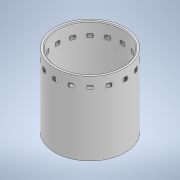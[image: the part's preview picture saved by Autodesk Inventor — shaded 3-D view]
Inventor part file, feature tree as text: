
AUTODESK INVENTOR PART (.ipt)
format: ipt  version: 2022.4 (Build 264492010, 492A)  size: 337,920 bytes
history: native  units: mm
features: extrude x2, sketch x2, fillet x1, chamfer x1, pattern_circular x1, plane x1
ambient origin geometry x8: Origin, YZ Plane, XZ Plane, XY Plane, X Axis, Y Axis, Z Axis, Center Point
bodies: Solid1 (feature_tree)
feature tree (8):
  extrude  "Extrusion1"  Depth=95.0mm TaperAngle=0.0deg
  extrude  "Extrusion3"  Depth=1.0mm
  fillet  "Fillet1"  [1 undecoded]
  chamfer  "Chamfer1"  Distance=10.0mm
  pattern_circular  "Circular Pattern2"  [2 undecoded]
  plane  "Work Plane1"
  sketch  "Sketch1"  dims[d0=84.05mm d2=95.0mm d3=0.0mm]
  sketch  "Sketch2"  dims[d4=5.0mm d5=5.0mm d8=45.0deg d9=10.0mm d10=6.0mm d11=0.0mm d12=1.0mm d16=1.0mm d17=2.0mm d18=45.0deg d19=160.0mm d20=360.0deg d24=43.0mm d38=3.5mm]
note: 3 required parameter values undecoded (feature->parameter linkage not recoverable at this tier; creation-order binding heuristic only, values carry confidence <= 0.55)
